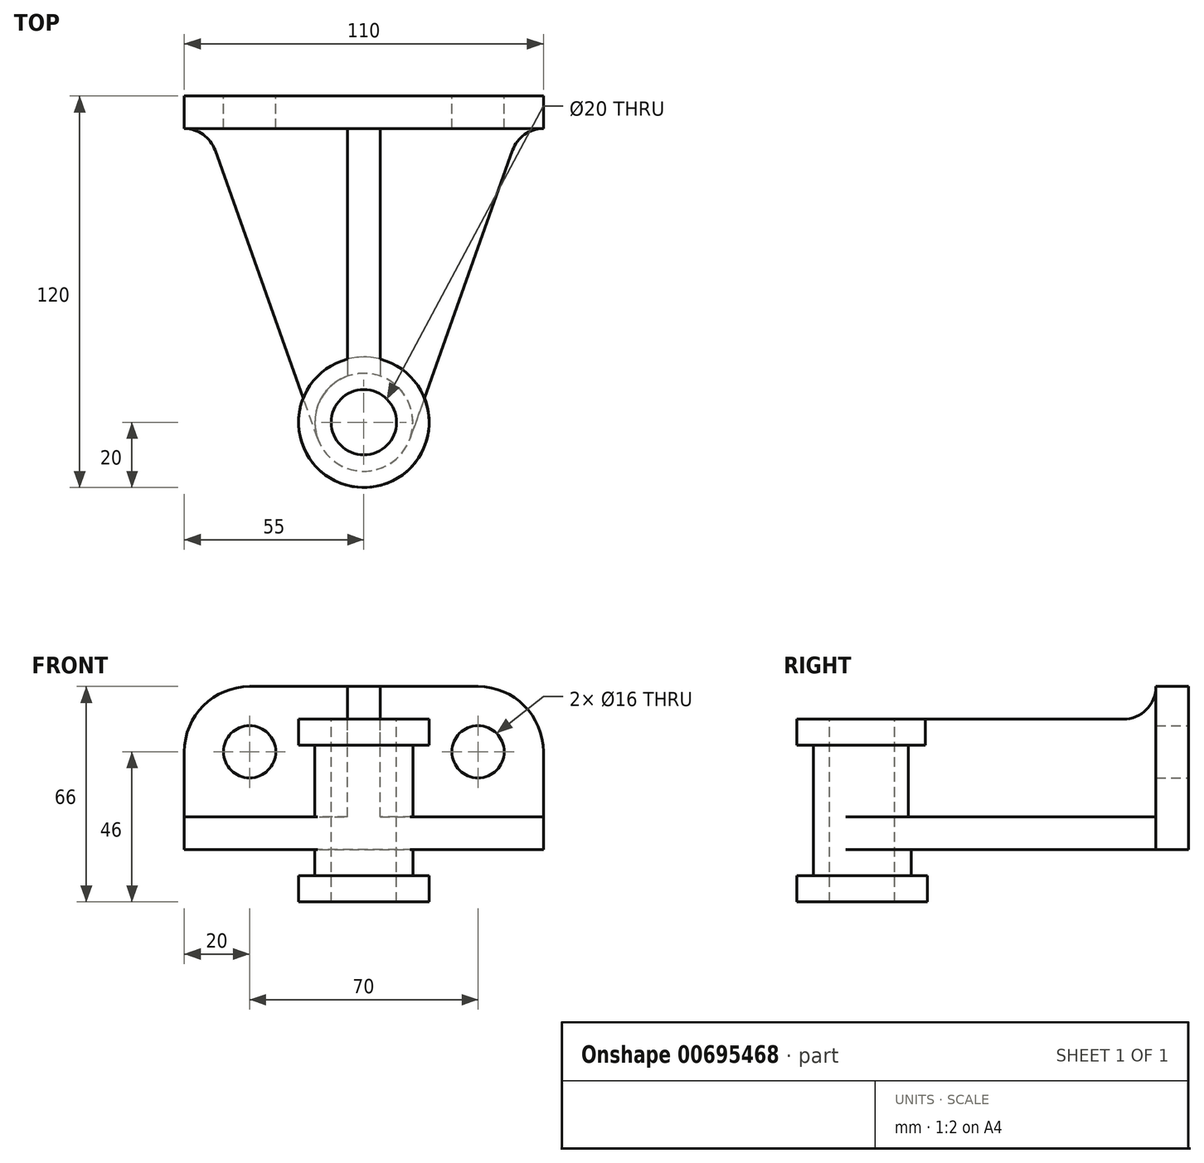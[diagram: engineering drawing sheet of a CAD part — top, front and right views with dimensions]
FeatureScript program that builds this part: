
annotation { "Feature Type Name" : "Feature", "Feature Type Description" : "" }
export const myFeature = defineFeature(function(context is Context, id is Id, definition is map)
    precondition{}
    {
        {
            var Q0;
            Q0=qCreatedBy(makeId("Front.planeOp"),FACE);
            var sketch = newSketch(context, id + "F0", { "sketchPlane" : qUnion([Q0])});
            skLineSegment(sketch, "E0.bottom", {"start": v(-55, 0) * mm, "end": v(55, 0) * mm});
            skLineSegment(sketch, "E0.top", {"start": v(-35, 50) * mm, "end": v(35, 50) * mm});
            skLineSegment(sketch, "E0.left", {"start": v(-55, 0) * mm, "end": v(-55, 30) * mm});
            skLineSegment(sketch, "E0.right", {"start": v(55, 0) * mm, "end": v(55, 30) * mm});
            skPoint(sketch, "E1.visualSharp", {"position": v(-55, 50) * mm});
            skArc(sketch, "E1.filletArc", {"start": v(-35, 50) * mm, "mid": v(-49.14, 44.14) * mm, "end": v(-55, 30) * mm});
            skPoint(sketch, "E2.visualSharp", {"position": v(55, 50) * mm});
            skArc(sketch, "E2.filletArc", {"start": v(55, 30) * mm, "mid": v(49.14, 44.14) * mm, "end": v(35, 50) * mm});
            skSolve(sketch);
        }
        {
            var Q0;
            Q0=makeQuery(id+"F0.imprint","IMPRINT",FACE,{"disambiguationData":[TD([[makeQuery(id+"F0.imprint","IMPRINT",EDGE,{"derivedFrom":sQuery(id+"F0.wireOp",EDGE,"E0.bottom")}),1.0]])]});
            extrude(context, id + "F1", {"entities" : qUnion([Q0]), "depth" : 10 * mm, "offsetDistance" : 25 * mm});
        }
        {
            var Q0;
            Q0=qCreatedBy(makeId("Top.planeOp"),FACE);
            cPlane(context, id + "F2", {"entities" : qUnion([Q0]), "cplaneType" : CPlaneType.OFFSET, "offset" : 10 * mm, "width" : 150 * mm, "height" : 150 * mm});
        }
        {
            var Q0;
            Q0=qCreatedBy(id+"F2.planeOp",FACE);
            var sketch = newSketch(context, id + "F3", { "sketchPlane" : qUnion([Q0])});
            skArc(sketch, "E3", {"start": v(-14.13, -105.03) * mm, "mid": v(0, -115) * mm, "end": v(14.13, -105.03) * mm});
            skPoint(sketch, "E4.0", {"position": v(-55, -10) * mm});
            skPoint(sketch, "E4.1", {"position": v(55, -10) * mm});
            skArc(sketch, "E5", {"start": v(-45.58, -16.65) * mm, "mid": v(-49.23, -11.83) * mm, "end": v(-55, -10) * mm});
            skLineSegment(sketch, "E6", {"start": v(-15.92, -100) * mm, "end": v(-45.58, -16.65) * mm});
            skArc(sketch, "E7.MirrorCS", {"start": v(45.58, -16.65) * mm, "mid": v(49.23, -11.83) * mm, "end": v(55, -10) * mm});
            skLineSegment(sketch, "E8.MirrorCS", {"start": v(15.92, -100) * mm, "end": v(45.58, -16.65) * mm});
            skLineSegment(sketch, "E9", {"start": v(-55, -10) * mm, "end": v(55, -10) * mm});
            skLineSegment(sketch, "E10", {"start": v(-15.92, -100) * mm, "end": v(-14.13, -105.03) * mm});
            skLineSegment(sketch, "E11", {"start": v(15.92, -100) * mm, "end": v(14.13, -105.03) * mm});
            skSolve(sketch);
        }
        {
            var Q0;
            Q0=makeQuery(id+"F3.imprint","IMPRINT",FACE,{"disambiguationData":[TD([[makeQuery(id+"F3.imprint","IMPRINT",EDGE,{"derivedFrom":sQuery(id+"F3.wireOp",EDGE,"E3")}),1.0]])]});
            extrude(context, id + "F4", {"entities" : qUnion([Q0]), "operationType" : NewBodyOperationType.ADD, "oppositeDirection" : true, "depth" : 10 * mm, "offsetDistance" : 25 * mm});
        }
        {
            var Q0;
            Q0=qCreatedBy(makeId("Right.planeOp"),FACE);
            var sketch = newSketch(context, id + "F5", { "sketchPlane" : qUnion([Q0])});
            skPoint(sketch, "E12.0", {"position": v(-10, 10) * mm});
            skLineSegment(sketch, "E13.bottom", {"start": v(-10, 10) * mm, "end": v(-100, 10) * mm});
            skLineSegment(sketch, "E13.top", {"start": v(-20, 40) * mm, "end": v(-100, 40) * mm});
            skLineSegment(sketch, "E13.left", {"start": v(-10, 10) * mm, "end": v(-10, 40) * mm});
            skLineSegment(sketch, "E13.right", {"start": v(-100, 10) * mm, "end": v(-100, 40) * mm});
            skLineSegment(sketch, "E14.0", {"start": v(-10, 50) * mm, "end": v(-10, 50) * mm});
            skPoint(sketch, "E15.newPointA", {"position": v(-10, 30) * mm});
            skArc(sketch, "E15.filletArc", {"start": v(-20, 40) * mm, "mid": v(-12.93, 42.93) * mm, "end": v(-10, 50) * mm});
            skLineSegment(sketch, "E16", {"start": v(-10, 50) * mm, "end": v(-10, 10) * mm});
            skSolve(sketch);
        }
        {
            var Q0;
            Q0=makeQuery(id+"F5.imprint","IMPRINT",FACE,{"disambiguationData":[TD([[makeQuery(id+"F5.imprint","IMPRINT",EDGE,{"derivedFrom":sQuery(id+"F5.wireOp",EDGE,"E13.bottom")}),-1.0]])]});
            extrude(context, id + "F6", {"entities" : qUnion([Q0]), "operationType" : NewBodyOperationType.ADD, "depth" : 10 * mm, "offsetDistance" : 25 * mm, "symmetric" : true});
        }
        {
            var Q0;
            Q0=makeQuery(id+"F6.opExtrude","SWEPT_FACE",FACE,{"disambiguationData":[OSD([sQuery(id+"F5.wireOp",EDGE,"E13.top")])]});
            var sketch = newSketch(context, id + "F7", { "sketchPlane" : qUnion([Q0])});
            skCircle(sketch, "E17", {"center": v(0, -100) * mm, "radius": 15 * mm});
            skSolve(sketch);
        }
        {
            var Q0;
            {var subQ1=sQuery(id+"F5.wireOp",EDGE,"E13.top");var subQ6=makeQuery(id+"F6.opExtrude","SWEPT_EDGE",EDGE,{"disambiguationData":[OSD([subQ1,sQuery(id+"F5.wireOp",EDGE,"E13.right")])]});Q0=makeQuery(id+"F7.imprint","IMPRINT",FACE,{"disambiguationData":[TD([[makeQuery(id+"F7.imprint","IMPRINT",EDGE,{"derivedFrom":subQ6}),1.0]])]});}
            var Q1;
            {var subQ1=sQuery(id+"F5.wireOp",EDGE,"E13.top");var subQ6=makeQuery(id+"F6.opExtrude","SWEPT_EDGE",EDGE,{"disambiguationData":[OSD([subQ1,sQuery(id+"F5.wireOp",EDGE,"E13.right")])]});Q1=makeQuery(id+"F7.imprint","IMPRINT",FACE,{"disambiguationData":[TD([[makeQuery(id+"F7.imprint","IMPRINT",EDGE,{"derivedFrom":subQ6}),-1.0]])]});}
            extrude(context, id + "F8", {"entities" : qUnion([Q0, Q1]), "operationType" : NewBodyOperationType.ADD, "oppositeDirection" : true, "depth" : 56 * mm, "offsetDistance" : 25 * mm});
        }
        {
            var Q0;
            {var subQ0=sQuery(id+"F5.wireOp",EDGE,"E13.top");Q0=makeQuery(id+"F8.boolean.opBoolean","MERGE",FACE,{"derivedFrom":[makeQuery(id+"F6.opExtrude","SWEPT_FACE",FACE,{"disambiguationData":[OSD([subQ0])]}),makeQuery(id+"F8.opExtrude","CAP_FACE",FACE,{"disambiguationData":[OSD([subQ0,sQuery(id+"F5.wireOp",EDGE,"E13.right"),sQuery(id+"F7.wireOp",EDGE,"E17")])],"isStart":true})]});}
            var sketch = newSketch(context, id + "F9", { "sketchPlane" : qUnion([Q0])});
            skCircle(sketch, "E18", {"center": v(0, -100) * mm, "radius": 20 * mm});
            skSolve(sketch);
        }
        {
            var Q0;
            {var subQ6=makeQuery(id+"F8.opExtrude","CAP_EDGE",EDGE,{"disambiguationData":[OSD([sQuery(id+"F7.wireOp",EDGE,"E17")])],"isStart":true});Q0=makeQuery(id+"F9.imprint","IMPRINT",FACE,{"disambiguationData":[TD([[makeQuery(id+"F9.imprint","IMPRINT",EDGE,{"derivedFrom":subQ6}),-1.0]])]});}
            var Q1;
            Q1=sQuery(id+"F9.wireOp",EDGE,"E18");
            extrude(context, id + "F10", {"entities" : qUnion([Q0]), "operationType" : NewBodyOperationType.ADD, "surfaceEntities" : qUnion([Q1]), "oppositeDirection" : true, "depth" : 8 * mm, "offsetDistance" : 25 * mm});
        }
        {
            var Q0;
            Q0=makeQuery(id+"F8.opExtrude","CAP_FACE",FACE,{"disambiguationData":[OSD([sQuery(id+"F7.wireOp",EDGE,"E17")])],"isStart":false});
            var sketch = newSketch(context, id + "F11", { "sketchPlane" : qUnion([Q0])});
            skCircle(sketch, "E19", {"center": v(0, 100) * mm, "radius": 20 * mm});
            skSolve(sketch);
        }
        {
            var Q0;
            Q0=makeQuery(id+"F11.imprint","IMPRINT",FACE,{"disambiguationData":[TD([[makeQuery(id+"F11.imprint","IMPRINT",EDGE,{"derivedFrom":sQuery(id+"F11.wireOp",EDGE,"E19")}),1.0]])]});
            var Q1;
            Q1=makeQuery(id+"F11.imprint","IMPRINT",FACE,{"disambiguationData":[TD([[makeQuery(id+"F11.imprint","IMPRINT",EDGE,{"derivedFrom":makeQuery(id+"F8.opExtrude","CAP_EDGE",EDGE,{"disambiguationData":[OSD([sQuery(id+"F7.wireOp",EDGE,"E17")])],"isStart":false})}),-1.0]])]});
            extrude(context, id + "F12", {"entities" : qUnion([Q0, Q1]), "operationType" : NewBodyOperationType.ADD, "oppositeDirection" : true, "depth" : 8 * mm, "offsetDistance" : 25 * mm});
        }
        {
            var Q0;
            {var subQ0=sQuery(id+"F7.wireOp",EDGE,"E17");var subQ1=sQuery(id+"F5.wireOp",EDGE,"E13.top");Q0=makeQuery(id+"F10.boolean.opBoolean","MERGE",FACE,{"derivedFrom":[makeQuery(id+"F8.boolean.opBoolean","MERGE",FACE,{"derivedFrom":[makeQuery(id+"F6.opExtrude","SWEPT_FACE",FACE,{"disambiguationData":[OSD([subQ1])]}),makeQuery(id+"F8.opExtrude","CAP_FACE",FACE,{"disambiguationData":[OSD([subQ0])],"isStart":true})]}),makeQuery(id+"F10.opExtrude","CAP_FACE",FACE,{"disambiguationData":[OSD([subQ1,subQ0,sQuery(id+"F9.wireOp",EDGE,"E18")])],"isStart":true})]});}
            var sketch = newSketch(context, id + "F13", { "sketchPlane" : qUnion([Q0])});
            skCircle(sketch, "E20", {"center": v(0, -100) * mm, "radius": 10 * mm});
            skSolve(sketch);
        }
        {
            var Q0;
            Q0=makeQuery(id+"F13.imprint","IMPRINT",FACE,{"disambiguationData":[TD([[makeQuery(id+"F13.imprint","IMPRINT",EDGE,{"derivedFrom":sQuery(id+"F13.wireOp",EDGE,"E20")}),1.0]])]});
            extrude(context, id + "F14", {"entities" : qUnion([Q0]), "operationType" : NewBodyOperationType.REMOVE, "endBound" : BoundingType.THROUGH_ALL, "oppositeDirection" : true, "depth" : 25 * mm, "offsetDistance" : 25 * mm});
        }
        {
            var Q0;
            Q0=makeQuery(id+"F1.opExtrude","CAP_FACE",FACE,{"disambiguationData":[OSD([sQuery(id+"F0.wireOp",EDGE,"E0.bottom"),sQuery(id+"F0.wireOp",EDGE,"E0.top"),sQuery(id+"F0.wireOp",EDGE,"E0.left"),sQuery(id+"F0.wireOp",EDGE,"E0.right"),sQuery(id+"F0.wireOp",EDGE,"E1.filletArc"),sQuery(id+"F0.wireOp",EDGE,"E2.filletArc")])],"isStart":true});
            var sketch = newSketch(context, id + "F15", { "sketchPlane" : qUnion([Q0])});
            skCircle(sketch, "E21", {"center": v(-35, 30) * mm, "radius": 8 * mm});
            skCircle(sketch, "E22", {"center": v(35, 30) * mm, "radius": 8 * mm});
            skSolve(sketch);
        }
        {
            var Q0;
            Q0=makeQuery(id+"F15.imprint","IMPRINT",FACE,{"disambiguationData":[TD([[makeQuery(id+"F15.imprint","IMPRINT",EDGE,{"derivedFrom":sQuery(id+"F15.wireOp",EDGE,"E21")}),1.0]])]});
            var Q1;
            Q1=makeQuery(id+"F15.imprint","IMPRINT",FACE,{"disambiguationData":[TD([[makeQuery(id+"F15.imprint","IMPRINT",EDGE,{"derivedFrom":sQuery(id+"F15.wireOp",EDGE,"E22")}),1.0]])]});
            var Q2;
            {var subQ1=sQuery(id+"F0.wireOp",EDGE,"E2.filletArc");var subQ2=sQuery(id+"F0.wireOp",EDGE,"E0.right");var subQ4=sQuery(id+"F0.wireOp",EDGE,"E0.top");Q2=makeQuery(id+"F6.boolean.opBoolean","SPLIT",FACE,{"disambiguationData":[TD([makeQuery(id+"F1.opExtrude","SWEPT_FACE",FACE,{"disambiguationData":[OSD([subQ2])]})])],"derivedFrom":makeQuery(id+"F1.opExtrude","CAP_FACE",FACE,{"disambiguationData":[OSD([sQuery(id+"F0.wireOp",EDGE,"E0.bottom"),subQ4,sQuery(id+"F0.wireOp",EDGE,"E0.left"),subQ2,sQuery(id+"F0.wireOp",EDGE,"E1.filletArc"),subQ1])],"isStart":false})});}
            extrude(context, id + "F16", {"entities" : qUnion([Q0, Q1]), "operationType" : NewBodyOperationType.REMOVE, "endBound" : BoundingType.UP_TO_SURFACE, "oppositeDirection" : true, "depth" : 25 * mm, "endBoundEntityFace" : qUnion([Q2]), "offsetDistance" : 25 * mm});
        }
    });
